# Revit family: Haworth_UniGroupToo_Post
name_source: partatom
category: Furniture Systems
revit_build: Autodesk Revit 2018 (Build: 20170223_1515(x64)
units: mm (PartAtom-declared; Revit-internal decimal feet)

## family parameters
Always vertical = Yes
Cut with Voids When Loaded = No
OmniClass Number = 23.40.70.14.64.21
OmniClass Title = Systems Furniture
Part Type = Normal
Room Calculation Point = No
Round Connector Dimension = Use Diameter
Shared = No
Work Plane-Based = No

## types (5) — shared parameters
Actual Width = 2"
Assembly Code = E2020500
Description = Haworth - Compose - Panel Accessories - Post
Manufacturer = Haworth
Max. Height = 90"
Max. Width = 3"
Min. Height = 29"
Min. Width = 3"
Min/Max Height = 29, 34, 42, 50, 58, 66, 74, 82, 90 in.
Model = Haworth - Compose - Panel Accessories - Post
Post Depth = 2"
Post Finish = Haworth _ Metal _ Brushed Aluminum
Revision Number = 4
Size = Verify Final Dim. w/ Haworth
Sustainability Info = http://www.haworth.com
Top Trim Thin Profile = Yes
Top Trim Width = 1/2"
Trim Finish = Haworth _ Metal _ Brushed Aluminum
URL = www.haworth.com
URL - Product = http://www.haworth.com
Warranty = http://www.haworth.com

## per-type parameters (varying)
| type | 120 Degree Post | 120 Degree Trim | Actual Height | Custom Size | Height | Square Post | Square Trim |
| 2-Way Intersection | No | No | 41 7/8" | No | 42" | Yes | Yes |
| 3-Way Intersection | No | No | 41 7/8" | No | 42" | Yes | Yes |
| 4-Way Intersection | No | No | 47 7/8" | Yes | 48" | Yes | Yes |
| 2-Way Intersection - 120 | Yes | Yes | 41 7/8" | No | 42" | No | No |
| 3-Way Intersection - 120 | Yes | Yes | 41 7/8" | No | 42" | No | No |

## geometry (parser evidence)
native form markers: Sweep x3
no freeform markers — native parametric forms only
